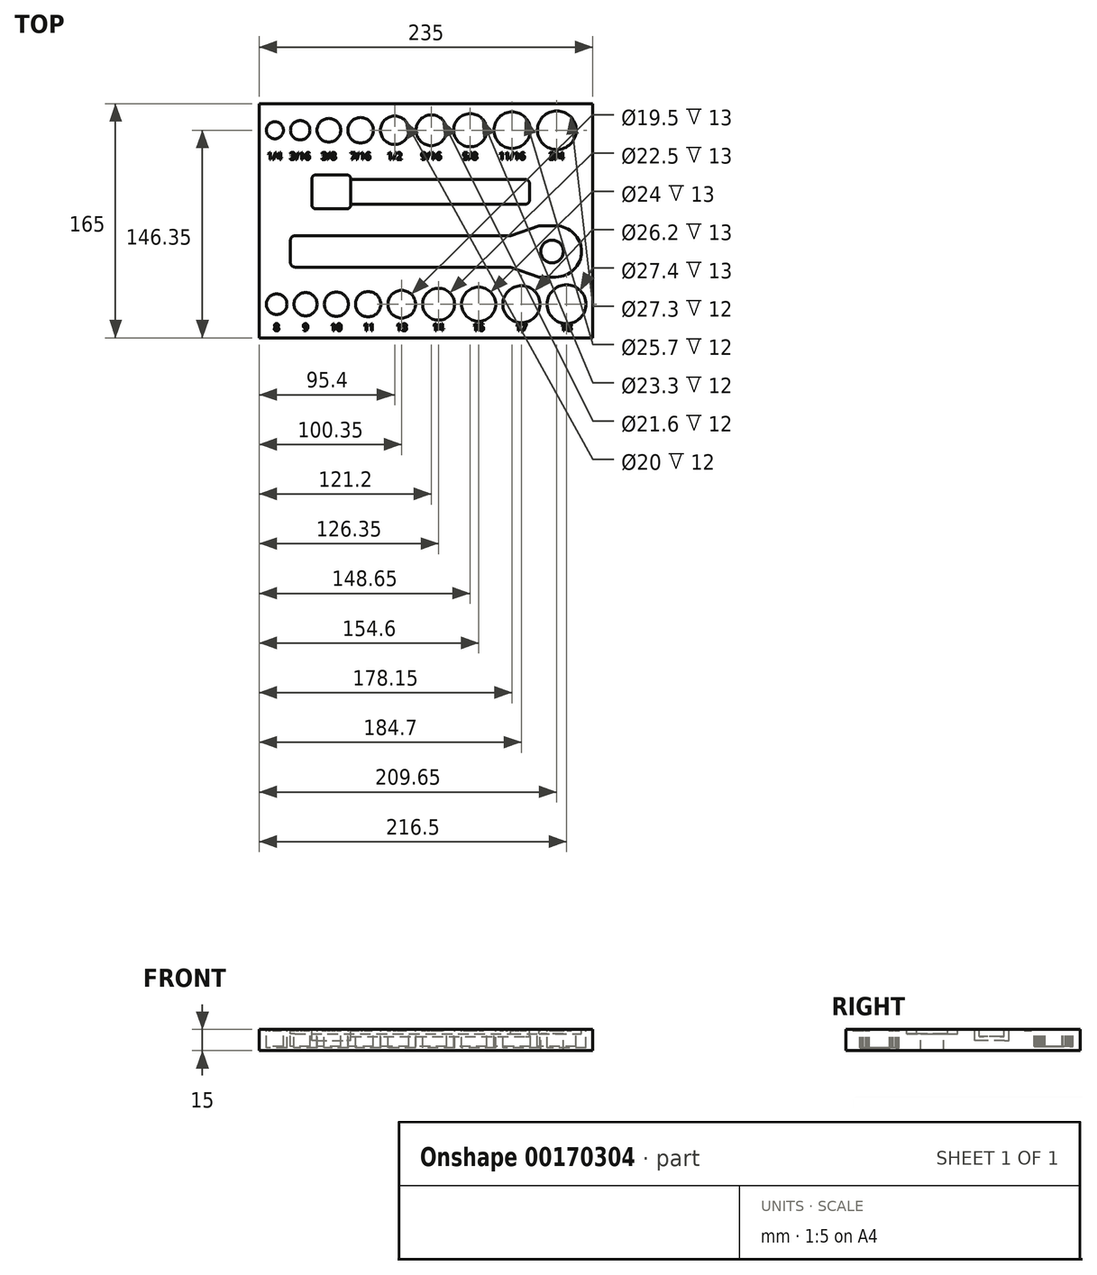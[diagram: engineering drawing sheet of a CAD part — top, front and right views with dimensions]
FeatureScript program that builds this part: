
annotation { "Feature Type Name" : "Feature", "Feature Type Description" : "" }
export const myFeature = defineFeature(function(context is Context, id is Id, definition is map)
    precondition{}
    {
        {
            var Q0;
            Q0=qCreatedBy(makeId("Top.planeOp"),FACE);
            var sketch = newSketch(context, id + "F0", { "sketchPlane" : qUnion([Q0])});
            skLineSegment(sketch, "E0.bottom", {"start": v(0, 0) * mm, "end": v(235, 0) * mm});
            skLineSegment(sketch, "E0.top", {"start": v(0, 165) * mm, "end": v(235, 165) * mm});
            skLineSegment(sketch, "E0.left", {"start": v(0, 0) * mm, "end": v(0, 165) * mm});
            skLineSegment(sketch, "E0.right", {"start": v(235, 0) * mm, "end": v(235, 165) * mm});
            skSolve(sketch);
        }
        {
            var Q0;
            Q0=makeQuery(id+"F0.imprint","IMPRINT",FACE,{"disambiguationData":[TD([[makeQuery(id+"F0.imprint","IMPRINT",EDGE,{"derivedFrom":sQuery(id+"F0.wireOp",EDGE,"E0.bottom")}),1.0]])]});
            extrude(context, id + "F1", {"entities" : qUnion([Q0]), "depth" : 15 * mm});
        }
        {
            var Q0;
            Q0=makeQuery(id+"F1.opExtrude","CAP_FACE",FACE,{"disambiguationData":[OSD([sQuery(id+"F0.wireOp",EDGE,"E0.bottom"),sQuery(id+"F0.wireOp",EDGE,"E0.top"),sQuery(id+"F0.wireOp",EDGE,"E0.left"),sQuery(id+"F0.wireOp",EDGE,"E0.right")])],"isStart":false});
            var sketch = newSketch(context, id + "F2", { "sketchPlane" : qUnion([Q0])});
            skLineSegment(sketch, "E1.bottom", {"start": v(0, 0) * mm, "end": v(12.25, 0) * mm, "construction": true});
            skLineSegment(sketch, "E1.top", {"start": v(0, 23.7) * mm, "end": v(12.25, 23.7) * mm, "construction": true});
            skLineSegment(sketch, "E1.left", {"start": v(0, 0) * mm, "end": v(0, 23.7) * mm, "construction": true});
            skLineSegment(sketch, "E1.right", {"start": v(12.25, 0) * mm, "end": v(12.25, 23.7) * mm, "construction": true});
            skLineSegment(sketch, "E2", {"start": v(12.25, 23.7) * mm, "end": v(32.65, 23.7) * mm, "construction": true});
            skLineSegment(sketch, "E3", {"start": v(32.65, 23.7) * mm, "end": v(54.3, 23.7) * mm, "construction": true});
            skPoint(sketch, "E3.endSnap0", {"position": v(22.45, 23.7) * mm});
            skLineSegment(sketch, "E4", {"start": v(54.3, 23.7) * mm, "end": v(76.7, 23.7) * mm, "construction": true});
            skLineSegment(sketch, "E5", {"start": v(76.7, 23.7) * mm, "end": v(100.35, 23.7) * mm, "construction": true});
            skLineSegment(sketch, "E6", {"start": v(100.35, 23.7) * mm, "end": v(126.35, 23.7) * mm, "construction": true});
            skLineSegment(sketch, "E7", {"start": v(126.35, 23.7) * mm, "end": v(154.6, 23.7) * mm, "construction": true});
            skLineSegment(sketch, "E8", {"start": v(154.6, 23.7) * mm, "end": v(184.7, 23.7) * mm, "construction": true});
            skLineSegment(sketch, "E9", {"start": v(184.7, 23.7) * mm, "end": v(216.5, 23.7) * mm, "construction": true});
            skCircle(sketch, "E10", {"center": v(12.25, 23.7) * mm, "radius": 7.25 * mm});
            skCircle(sketch, "E11", {"center": v(32.65, 23.7) * mm, "radius": 8.15 * mm});
            skCircle(sketch, "E12", {"center": v(54.3, 23.7) * mm, "radius": 8.5 * mm});
            skCircle(sketch, "E13", {"center": v(76.7, 23.7) * mm, "radius": 8.9 * mm});
            skCircle(sketch, "E14", {"center": v(100.35, 23.7) * mm, "radius": 9.75 * mm});
            skCircle(sketch, "E15", {"center": v(126.35, 23.7) * mm, "radius": 11.25 * mm});
            skCircle(sketch, "E16", {"center": v(154.6, 23.7) * mm, "radius": 12 * mm});
            skCircle(sketch, "E17", {"center": v(184.7, 23.7) * mm, "radius": 13.1 * mm});
            skCircle(sketch, "E18", {"center": v(216.5, 23.7) * mm, "radius": 13.7 * mm});
            skSolve(sketch);
        }
        {
            var Q0;
            Q0=makeQuery(id+"F2.imprint","IMPRINT",FACE,{"disambiguationData":[TD([[makeQuery(id+"F2.imprint","IMPRINT",EDGE,{"derivedFrom":sQuery(id+"F2.wireOp",EDGE,"E10")}),1.0]])]});
            var Q1;
            Q1=makeQuery(id+"F2.imprint","IMPRINT",FACE,{"disambiguationData":[TD([[makeQuery(id+"F2.imprint","IMPRINT",EDGE,{"derivedFrom":sQuery(id+"F2.wireOp",EDGE,"E18")}),1.0]])]});
            var Q2;
            Q2=makeQuery(id+"F2.imprint","IMPRINT",FACE,{"disambiguationData":[TD([[makeQuery(id+"F2.imprint","IMPRINT",EDGE,{"derivedFrom":sQuery(id+"F2.wireOp",EDGE,"E17")}),1.0]])]});
            var Q3;
            Q3=makeQuery(id+"F2.imprint","IMPRINT",FACE,{"disambiguationData":[TD([[makeQuery(id+"F2.imprint","IMPRINT",EDGE,{"derivedFrom":sQuery(id+"F2.wireOp",EDGE,"E16")}),1.0]])]});
            var Q4;
            Q4=makeQuery(id+"F2.imprint","IMPRINT",FACE,{"disambiguationData":[TD([[makeQuery(id+"F2.imprint","IMPRINT",EDGE,{"derivedFrom":sQuery(id+"F2.wireOp",EDGE,"E15")}),1.0]])]});
            var Q5;
            Q5=makeQuery(id+"F2.imprint","IMPRINT",FACE,{"disambiguationData":[TD([[makeQuery(id+"F2.imprint","IMPRINT",EDGE,{"derivedFrom":sQuery(id+"F2.wireOp",EDGE,"E14")}),1.0]])]});
            var Q6;
            Q6=makeQuery(id+"F2.imprint","IMPRINT",FACE,{"disambiguationData":[TD([[makeQuery(id+"F2.imprint","IMPRINT",EDGE,{"derivedFrom":sQuery(id+"F2.wireOp",EDGE,"E13")}),1.0]])]});
            var Q7;
            Q7=makeQuery(id+"F2.imprint","IMPRINT",FACE,{"disambiguationData":[TD([[makeQuery(id+"F2.imprint","IMPRINT",EDGE,{"derivedFrom":sQuery(id+"F2.wireOp",EDGE,"E12")}),1.0]])]});
            var Q8;
            Q8=makeQuery(id+"F2.imprint","IMPRINT",FACE,{"disambiguationData":[TD([[makeQuery(id+"F2.imprint","IMPRINT",EDGE,{"derivedFrom":sQuery(id+"F2.wireOp",EDGE,"E11")}),1.0]])]});
            extrude(context, id + "F3", {"entities" : qUnion([Q0, Q1, Q2, Q3, Q4, Q5, Q6, Q7, Q8]), "operationType" : NewBodyOperationType.REMOVE, "oppositeDirection" : true, "depth" : 13 * mm});
        }
        {
            var Q0;
            Q0=makeQuery(id+"F1.opExtrude","CAP_FACE",FACE,{"disambiguationData":[OSD([sQuery(id+"F0.wireOp",EDGE,"E0.bottom"),sQuery(id+"F0.wireOp",EDGE,"E0.top"),sQuery(id+"F0.wireOp",EDGE,"E0.left"),sQuery(id+"F0.wireOp",EDGE,"E0.right")])],"isStart":false});
            var sketch = newSketch(context, id + "F4", { "sketchPlane" : qUnion([Q0])});
            skLineSegment(sketch, "E19", {"start": v(0, 0) * mm, "end": v(0, 3) * mm, "construction": true});
            skLineSegment(sketch, "E20", {"start": v(0, 3) * mm, "end": v(235, 3) * mm, "construction": true});
            skLineSegment(sketch, "E21", {"start": v(235, 3) * mm, "end": v(216.5, 23.7) * mm, "construction": true});
            skLineSegment(sketch, "E22", {"start": v(216.5, 23.7) * mm, "end": v(216.5, 3) * mm, "construction": true});
            skLineSegment(sketch, "E23", {"start": v(216.5, 3) * mm, "end": v(184.7, 23.7) * mm, "construction": true});
            skLineSegment(sketch, "E24", {"start": v(184.7, 23.7) * mm, "end": v(184.7, 3) * mm, "construction": true});
            skLineSegment(sketch, "E25", {"start": v(184.7, 3) * mm, "end": v(154.6, 23.7) * mm, "construction": true});
            skLineSegment(sketch, "E26", {"start": v(154.6, 23.7) * mm, "end": v(154.6, 3) * mm, "construction": true});
            skLineSegment(sketch, "E27", {"start": v(154.6, 3) * mm, "end": v(126.35, 23.7) * mm, "construction": true});
            skLineSegment(sketch, "E28", {"start": v(126.35, 23.7) * mm, "end": v(126.35, 3) * mm, "construction": true});
            skLineSegment(sketch, "E29", {"start": v(126.35, 3) * mm, "end": v(100.35, 23.7) * mm, "construction": true});
            skLineSegment(sketch, "E30", {"start": v(100.35, 23.7) * mm, "end": v(100.35, 3) * mm, "construction": true});
            skLineSegment(sketch, "E31", {"start": v(100.35, 3) * mm, "end": v(76.7, 23.7) * mm, "construction": true});
            skLineSegment(sketch, "E32", {"start": v(76.7, 23.7) * mm, "end": v(76.7, 3) * mm, "construction": true});
            skLineSegment(sketch, "E33", {"start": v(76.7, 3) * mm, "end": v(54.3, 23.7) * mm, "construction": true});
            skLineSegment(sketch, "E34", {"start": v(54.3, 23.7) * mm, "end": v(54.3, 3) * mm, "construction": true});
            skLineSegment(sketch, "E35", {"start": v(54.3, 3) * mm, "end": v(32.65, 23.7) * mm, "construction": true});
            skLineSegment(sketch, "E36", {"start": v(32.65, 23.7) * mm, "end": v(32.65, 3) * mm, "construction": true});
            skLineSegment(sketch, "E37", {"start": v(32.65, 3) * mm, "end": v(12.25, 23.7) * mm, "construction": true});
            skLineSegment(sketch, "E38", {"start": v(12.25, 23.7) * mm, "end": v(12.25, 3) * mm, "construction": true});
            skSolve(sketch);
        }
        {
            var Q0;
            Q0=makeQuery(id+"F4.imprint","IMPRINT",FACE,{"disambiguationData":[TD([[makeQuery(id+"F4.imprint","IMPRINT",EDGE,{"derivedFrom":makeQuery(id+"F1.opExtrude","CAP_EDGE",EDGE,{"disambiguationData":[OSD([sQuery(id+"F0.wireOp",EDGE,"E0.bottom")])],"isStart":false})}),1.0]])]});
            var sketch = newSketch(context, id + "F5", { "sketchPlane" : qUnion([Q0])});
            skText(sketch, "E39", { "text": "8", "fontName": "OpenSans-Regular.ttf"});
            skText(sketch, "E40", { "text": "9", "fontName": "OpenSans-Regular.ttf"});
            skText(sketch, "E41", { "text": "10", "fontName": "OpenSans-Regular.ttf"});
            skText(sketch, "E42", { "text": "11", "fontName": "OpenSans-Regular.ttf"});
            skText(sketch, "E43", { "text": "13", "fontName": "OpenSans-Regular.ttf"});
            skText(sketch, "E44", { "text": "14", "fontName": "OpenSans-Regular.ttf"});
            skText(sketch, "E45", { "text": "16", "fontName": "OpenSans-Regular.ttf"});
            skText(sketch, "E46", { "text": "17", "fontName": "OpenSans-Regular.ttf"});
            skText(sketch, "E47", { "text": "18", "fontName": "OpenSans-Regular.ttf"});
            const initialGuessF5  = {"E39": [0.01022, 0.005, 1, 0, 0.005], "E40": [0.03063, 0.005, 1, 0, 0.005], "E41": [0.05028, 0.005, 1, 0, 0.005], "E42": [0.07328, 0.005, 1, 0, 0.005], "E43": [0.09636, 0.005, 1, 0, 0.005], "E44": [0.12222, 0.005, 1, 0, 0.005], "E45": [0.15057, 0.005, 1, 0, 0.005], "E46": [0.18068, 0.005, 1, 0, 0.005], "E47": [0.21248, 0.005, 1, 0, 0.005]};
            skSetInitialGuess(sketch, initialGuessF5);
            skSolve(sketch);
        }
        {
            var Q0;
            Q0 = qSketchRegion(id + "F5", true);
            extrude(context, id + "F6", {"entities" : qUnion([Q0]), "operationType" : NewBodyOperationType.REMOVE, "oppositeDirection" : true, "depth" : 1 * mm});
        }
        {
            var Q0;
            Q0=makeQuery(id+"F4.imprint","IMPRINT",FACE,{"disambiguationData":[TD([[makeQuery(id+"F4.imprint","IMPRINT",EDGE,{"derivedFrom":makeQuery(id+"F1.opExtrude","CAP_EDGE",EDGE,{"disambiguationData":[OSD([sQuery(id+"F0.wireOp",EDGE,"E0.bottom")])],"isStart":false})}),1.0]])]});
            var sketch = newSketch(context, id + "F7", { "sketchPlane" : qUnion([Q0])});
            skCircle(sketch, "E48.0", {"center": v(12.25, 23.7) * mm, "radius": 7.25 * mm});
            skLineSegment(sketch, "E49", {"start": v(12.25, 23.7) * mm, "end": v(0, 23.7) * mm, "construction": true});
            skLineSegment(sketch, "E50", {"start": v(0, 23.7) * mm, "end": v(0, 60.9) * mm, "construction": true});
            skLineSegment(sketch, "E51", {"start": v(0, 60.9) * mm, "end": v(22, 60.9) * mm, "construction": true});
            skLineSegment(sketch, "E52.top", {"start": v(25, 71.9) * mm, "end": v(177, 71.9) * mm});
            skLineSegment(sketch, "E52.left", {"start": v(22, 60.9) * mm, "end": v(22, 68.9) * mm});
            skLineSegment(sketch, "E53.bottom", {"start": v(194.75, 71.9) * mm, "end": v(197, 71.9) * mm, "construction": true});
            skLineSegment(sketch, "E53.top", {"start": v(177, 78.9) * mm, "end": v(197, 78.9) * mm, "construction": true});
            skLineSegment(sketch, "E54", {"start": v(177, 71.9) * mm, "end": v(197, 78.9) * mm});
            skLineSegment(sketch, "E55", {"start": v(197, 78.9) * mm, "end": v(209, 78.9) * mm});
            skArc(sketch, "E56", {"start": v(227, 60.9) * mm, "mid": v(221.73, 73.63) * mm, "end": v(209, 78.9) * mm});
            skLineSegment(sketch, "E57.MirrorCS", {"start": v(22, 60.9) * mm, "end": v(22, 52.9) * mm});
            skLineSegment(sketch, "E58.MirrorCS", {"start": v(25, 49.9) * mm, "end": v(177, 49.9) * mm});
            skLineSegment(sketch, "E59.MirrorCS", {"start": v(177, 49.9) * mm, "end": v(197, 42.9) * mm});
            skLineSegment(sketch, "E60.MirrorCS", {"start": v(197, 42.9) * mm, "end": v(209, 42.9) * mm});
            skArc(sketch, "E61.MirrorCS", {"start": v(227, 60.9) * mm, "mid": v(221.73, 48.17) * mm, "end": v(209, 42.9) * mm});
            skPoint(sketch, "E62.visualSharp", {"position": v(22, 71.9) * mm});
            skArc(sketch, "E62.filletArc", {"start": v(25, 71.9) * mm, "mid": v(22.88, 71.02) * mm, "end": v(22, 68.9) * mm});
            skPoint(sketch, "E63.visualSharp", {"position": v(22, 49.9) * mm});
            skArc(sketch, "E63.filletArc", {"start": v(22, 52.9) * mm, "mid": v(22.88, 50.78) * mm, "end": v(25, 49.9) * mm});
            skLineSegment(sketch, "E64", {"start": v(227, 60.9) * mm, "end": v(206.25, 60.9) * mm, "construction": true});
            skCircle(sketch, "E65", {"center": v(206.25, 60.9) * mm, "radius": 8 * mm});
            skLineSegment(sketch, "E66", {"start": v(25, 71.9) * mm, "end": v(85, 71.9) * mm, "construction": true});
            skLineSegment(sketch, "E67.bottom", {"start": v(85, 71.9) * mm, "end": v(135, 71.9) * mm});
            skPoint(sketch, "E68.visualSharp", {"position": v(85, 81.9) * mm});
            skPoint(sketch, "E69.visualSharp", {"position": v(135, 81.9) * mm});
            skLineSegment(sketch, "E70", {"start": v(22, 60.9) * mm, "end": v(206.25, 60.9) * mm, "construction": true});
            skSolve(sketch);
        }
        {
            var Q0;
            Q0 = qSketchRegion(id + "F7", true);
            extrude(context, id + "F8", {"entities" : qUnion([Q0]), "operationType" : NewBodyOperationType.REMOVE, "oppositeDirection" : true, "depth" : 3 * mm});
        }
        {
            var Q0;
            Q0=makeQuery(id+"F4.imprint","IMPRINT",FACE,{"disambiguationData":[TD([[makeQuery(id+"F4.imprint","IMPRINT",EDGE,{"derivedFrom":makeQuery(id+"F1.opExtrude","CAP_EDGE",EDGE,{"disambiguationData":[OSD([sQuery(id+"F0.wireOp",EDGE,"E0.bottom")])],"isStart":false})}),1.0]])]});
            var sketch = newSketch(context, id + "F9", { "sketchPlane" : qUnion([Q0])});
            skCircle(sketch, "E71.0", {"center": v(206.25, 60.9) * mm, "radius": 8 * mm});
            skCircle(sketch, "E72", {"center": v(206.25, 60.9) * mm, "radius": 8.25 * mm});
            skSolve(sketch);
        }
        {
            var Q0;
            Q0=makeQuery(id+"F9.imprint","IMPRINT",FACE,{"disambiguationData":[TD([[makeQuery(id+"F9.imprint","IMPRINT",EDGE,{"derivedFrom":sQuery(id+"F9.wireOp",EDGE,"E71.0")}),1.0]])]});
            extrude(context, id + "F10", {"entities" : qUnion([Q0]), "operationType" : NewBodyOperationType.REMOVE, "oppositeDirection" : true, "depth" : 25 * mm});
        }
        {
            var Q0;
            Q0=makeQuery(id+"F4.imprint","IMPRINT",FACE,{"disambiguationData":[TD([[makeQuery(id+"F4.imprint","IMPRINT",EDGE,{"derivedFrom":makeQuery(id+"F1.opExtrude","CAP_EDGE",EDGE,{"disambiguationData":[OSD([sQuery(id+"F0.wireOp",EDGE,"E0.bottom")])],"isStart":false})}),1.0]])]});
            var sketch = newSketch(context, id + "F11", { "sketchPlane" : qUnion([Q0])});
            skPoint(sketch, "E73.0", {"position": v(22, 60.9) * mm});
            skLineSegment(sketch, "E74", {"start": v(22, 60.9) * mm, "end": v(0, 60.9) * mm, "construction": true});
            skLineSegment(sketch, "E75", {"start": v(0, 60.9) * mm, "end": v(0, 102.9) * mm, "construction": true});
            skLineSegment(sketch, "E76", {"start": v(0, 102.9) * mm, "end": v(37, 102.9) * mm, "construction": true});
            skLineSegment(sketch, "E77", {"start": v(190.5, 102.9) * mm, "end": v(239.14, 102.9) * mm, "construction": true});
            skLineSegment(sketch, "E78.top", {"start": v(40, 114.9) * mm, "end": v(61.5, 114.9) * mm});
            skLineSegment(sketch, "E78.left", {"start": v(37, 102.9) * mm, "end": v(37, 111.9) * mm});
            skLineSegment(sketch, "E78.right", {"start": v(64.5, 111.65) * mm, "end": v(64.5, 111.9) * mm});
            skLineSegment(sketch, "E79.top", {"start": v(64.5, 111.65) * mm, "end": v(187.5, 111.65) * mm});
            skLineSegment(sketch, "E79.right", {"start": v(190.5, 102.9) * mm, "end": v(190.5, 108.65) * mm});
            skPoint(sketch, "E80.visualSharp", {"position": v(64.5, 114.9) * mm});
            skArc(sketch, "E80.filletArc", {"start": v(64.5, 111.9) * mm, "mid": v(63.62, 114.02) * mm, "end": v(61.5, 114.9) * mm});
            skPoint(sketch, "E81.visualSharp", {"position": v(37, 114.9) * mm});
            skArc(sketch, "E81.filletArc", {"start": v(40, 114.9) * mm, "mid": v(37.88, 114.02) * mm, "end": v(37, 111.9) * mm});
            skPoint(sketch, "E82.visualSharp", {"position": v(190.5, 111.65) * mm});
            skArc(sketch, "E82.filletArc", {"start": v(190.5, 108.65) * mm, "mid": v(189.62, 110.77) * mm, "end": v(187.5, 111.65) * mm});
            skLineSegment(sketch, "E83.MirrorCS", {"start": v(37, 102.9) * mm, "end": v(37, 93.9) * mm});
            skArc(sketch, "E84.MirrorCS", {"start": v(40, 90.9) * mm, "mid": v(37.88, 91.78) * mm, "end": v(37, 93.9) * mm});
            skLineSegment(sketch, "E85.MirrorCS", {"start": v(40, 90.9) * mm, "end": v(61.5, 90.9) * mm});
            skArc(sketch, "E86.MirrorCS", {"start": v(64.5, 93.9) * mm, "mid": v(63.62, 91.78) * mm, "end": v(61.5, 90.9) * mm});
            skLineSegment(sketch, "E87.MirrorCS", {"start": v(64.5, 94.15) * mm, "end": v(64.5, 93.9) * mm});
            skLineSegment(sketch, "E88.MirrorCS", {"start": v(64.5, 94.15) * mm, "end": v(187.5, 94.15) * mm});
            skArc(sketch, "E89.MirrorCS", {"start": v(190.5, 97.15) * mm, "mid": v(189.62, 95.03) * mm, "end": v(187.5, 94.15) * mm});
            skLineSegment(sketch, "E90.MirrorCS", {"start": v(190.5, 102.9) * mm, "end": v(190.5, 97.15) * mm});
            skSolve(sketch);
        }
        {
            var Q0;
            Q0 = qSketchRegion(id + "F11", true);
            extrude(context, id + "F12", {"entities" : qUnion([Q0]), "operationType" : NewBodyOperationType.REMOVE, "oppositeDirection" : true, "depth" : 5 * mm});
        }
        {
            var Q0;
            Q0=makeQuery(id+"F4.imprint","IMPRINT",FACE,{"disambiguationData":[TD([[makeQuery(id+"F4.imprint","IMPRINT",EDGE,{"derivedFrom":makeQuery(id+"F1.opExtrude","CAP_EDGE",EDGE,{"disambiguationData":[OSD([sQuery(id+"F0.wireOp",EDGE,"E0.bottom")])],"isStart":false})}),1.0]])]});
            var sketch = newSketch(context, id + "F13", { "sketchPlane" : qUnion([Q0])});
            skLineSegment(sketch, "E91.top", {"start": v(5, 146.35) * mm, "end": v(11, 146.35) * mm, "construction": true});
            skLineSegment(sketch, "E92.0.1", {"start": v(0, 0) * mm, "end": v(235, 0) * mm});
            skLineSegment(sketch, "E92.0.2", {"start": v(235, 0) * mm, "end": v(235, 165) * mm});
            skLineSegment(sketch, "E92.0.3", {"start": v(235, 165) * mm, "end": v(0, 165) * mm});
            skLineSegment(sketch, "E93", {"start": v(11, 146.35) * mm, "end": v(28.85, 146.35) * mm, "construction": true});
            skLineSegment(sketch, "E94", {"start": v(28.85, 146.35) * mm, "end": v(49.05, 146.35) * mm, "construction": true});
            skLineSegment(sketch, "E95", {"start": v(49.05, 146.35) * mm, "end": v(71.4, 146.35) * mm, "construction": true});
            skLineSegment(sketch, "E96", {"start": v(71.4, 146.35) * mm, "end": v(95.4, 146.35) * mm, "construction": true});
            skLineSegment(sketch, "E97", {"start": v(95.4, 146.35) * mm, "end": v(121.2, 146.35) * mm, "construction": true});
            skLineSegment(sketch, "E98", {"start": v(121.2, 146.35) * mm, "end": v(148.65, 146.35) * mm, "construction": true});
            skLineSegment(sketch, "E99", {"start": v(148.65, 146.35) * mm, "end": v(178.15, 146.35) * mm, "construction": true});
            skLineSegment(sketch, "E100", {"start": v(178.15, 146.35) * mm, "end": v(209.65, 146.35) * mm, "construction": true});
            skCircle(sketch, "E101", {"center": v(11, 146.35) * mm, "radius": 6 * mm});
            skCircle(sketch, "E102", {"center": v(28.85, 146.35) * mm, "radius": 6.85 * mm});
            skCircle(sketch, "E103", {"center": v(49.05, 146.35) * mm, "radius": 8.35 * mm});
            skCircle(sketch, "E104", {"center": v(71.4, 146.35) * mm, "radius": 9 * mm});
            skCircle(sketch, "E105", {"center": v(95.4, 146.35) * mm, "radius": 10 * mm});
            skCircle(sketch, "E106", {"center": v(121.2, 146.35) * mm, "radius": 10.8 * mm});
            skCircle(sketch, "E107", {"center": v(148.65, 146.35) * mm, "radius": 11.65 * mm});
            skCircle(sketch, "E108", {"center": v(178.15, 146.35) * mm, "radius": 12.85 * mm});
            skCircle(sketch, "E109", {"center": v(209.65, 146.35) * mm, "radius": 13.65 * mm});
            skSolve(sketch);
        }
        {
            var Q0;
            Q0 = qSketchRegion(id + "F13", true);
            extrude(context, id + "F14", {"entities" : qUnion([Q0]), "operationType" : NewBodyOperationType.REMOVE, "oppositeDirection" : true, "depth" : 12 * mm});
        }
        {
            var Q0;
            Q0=makeQuery(id+"F4.imprint","IMPRINT",FACE,{"disambiguationData":[TD([[makeQuery(id+"F4.imprint","IMPRINT",EDGE,{"derivedFrom":makeQuery(id+"F1.opExtrude","CAP_EDGE",EDGE,{"disambiguationData":[OSD([sQuery(id+"F0.wireOp",EDGE,"E0.bottom")])],"isStart":false})}),1.0]])]});
            var sketch = newSketch(context, id + "F15", { "sketchPlane" : qUnion([Q0])});
            skLineSegment(sketch, "E110.0.1", {"start": v(0, 0) * mm, "end": v(235, 0) * mm});
            skLineSegment(sketch, "E110.0.2", {"start": v(235, 0) * mm, "end": v(235, 165) * mm});
            skCircle(sketch, "E111.0", {"center": v(11, 146.35) * mm, "radius": 6 * mm, "construction": true});
            skCircle(sketch, "E111.1", {"center": v(28.85, 146.35) * mm, "radius": 6.85 * mm, "construction": true});
            skCircle(sketch, "E111.2", {"center": v(49.05, 146.35) * mm, "radius": 8.35 * mm, "construction": true});
            skCircle(sketch, "E111.3", {"center": v(71.4, 146.35) * mm, "radius": 9 * mm, "construction": true});
            skCircle(sketch, "E111.4", {"center": v(95.4, 146.35) * mm, "radius": 10 * mm, "construction": true});
            skCircle(sketch, "E111.5", {"center": v(121.2, 146.35) * mm, "radius": 10.8 * mm, "construction": true});
            skCircle(sketch, "E111.6", {"center": v(148.65, 146.35) * mm, "radius": 11.65 * mm, "construction": true});
            skCircle(sketch, "E111.7", {"center": v(178.15, 146.35) * mm, "radius": 12.85 * mm, "construction": true});
            skCircle(sketch, "E111.8", {"center": v(209.65, 146.35) * mm, "radius": 13.65 * mm, "construction": true});
            skLineSegment(sketch, "E112", {"start": v(0, 125.7) * mm, "end": v(11, 146.35) * mm, "construction": true});
            skLineSegment(sketch, "E113", {"start": v(11, 125.7) * mm, "end": v(28.85, 146.35) * mm, "construction": true});
            skLineSegment(sketch, "E114", {"start": v(28.85, 125.7) * mm, "end": v(49.05, 146.35) * mm, "construction": true});
            skLineSegment(sketch, "E115", {"start": v(49.05, 125.7) * mm, "end": v(71.4, 146.35) * mm, "construction": true});
            skLineSegment(sketch, "E116", {"start": v(71.4, 125.7) * mm, "end": v(95.4, 146.35) * mm, "construction": true});
            skLineSegment(sketch, "E117", {"start": v(95.4, 125.7) * mm, "end": v(121.2, 146.35) * mm, "construction": true});
            skLineSegment(sketch, "E118", {"start": v(121.2, 125.7) * mm, "end": v(148.65, 146.35) * mm, "construction": true});
            skLineSegment(sketch, "E119", {"start": v(148.65, 125.7) * mm, "end": v(178.15, 146.35) * mm, "construction": true});
            skLineSegment(sketch, "E120", {"start": v(178.15, 125.7) * mm, "end": v(209.65, 146.35) * mm, "construction": true});
            skLineSegment(sketch, "E121", {"start": v(209.65, 146.35) * mm, "end": v(209.65, 125.7) * mm, "construction": true});
            skText(sketch, "E122", { "text": "1/4", "fontName": "OpenSans-Regular.ttf"});
            skText(sketch, "E123", { "text": "3/16", "fontName": "OpenSans-Regular.ttf"});
            skText(sketch, "E124", { "text": "3/8", "fontName": "OpenSans-Regular.ttf"});
            skText(sketch, "E125", { "text": "7/16", "fontName": "OpenSans-Regular.ttf"});
            skText(sketch, "E126", { "text": "1/2", "fontName": "OpenSans-Regular.ttf"});
            skText(sketch, "E127", { "text": "9/16", "fontName": "OpenSans-Regular.ttf"});
            skText(sketch, "E128", { "text": "5/8", "fontName": "OpenSans-Regular.ttf"});
            skText(sketch, "E129", { "text": "11/16", "fontName": "OpenSans-Regular.ttf"});
            skText(sketch, "E130", { "text": "3/4\n", "fontName": "OpenSans-Regular.ttf"});
            const initialGuessF15  = {"E122": [0.0056, 0.1257, 1, 0, 0.005], "E123": [0.02156, 0.1257, 1, 0, 0.005], "E124": [0.04376, 0.1257, 1, 0, 0.005], "E125": [0.06411, 0.1257, 1, 0, 0.005], "E126": [0.09012, 0.1257, 1, 0, 0.005], "E127": [0.11391, 0.1257, 1, 0, 0.005], "E128": [0.14336, 0.1257, 1, 0, 0.005], "E129": [0.16888, 0.1257, 1, 0, 0.005], "E130": [0.20425, 0.1257, 1, 0, 0.005]};
            skSetInitialGuess(sketch, initialGuessF15);
            skSolve(sketch);
        }
        {
            var Q0;
            Q0 = qSketchRegion(id + "F15", true);
            extrude(context, id + "F16", {"entities" : qUnion([Q0]), "operationType" : NewBodyOperationType.REMOVE, "oppositeDirection" : true, "depth" : 1 * mm});
        }
        {
            var Q0;
            Q0=makeQuery(id+"F4.imprint","IMPRINT",FACE,{"disambiguationData":[TD([[makeQuery(id+"F4.imprint","IMPRINT",EDGE,{"derivedFrom":makeQuery(id+"F1.opExtrude","CAP_EDGE",EDGE,{"disambiguationData":[OSD([sQuery(id+"F0.wireOp",EDGE,"E0.bottom")])],"isStart":false})}),1.0]])]});
            var sketch = newSketch(context, id + "F17", { "sketchPlane" : qUnion([Q0])});
            skLineSegment(sketch, "E131.0", {"start": v(40, 114.9) * mm, "end": v(61.5, 114.9) * mm});
            skArc(sketch, "E132.0", {"start": v(40, 114.9) * mm, "mid": v(37.88, 114.02) * mm, "end": v(37, 111.9) * mm});
            skLineSegment(sketch, "E133.0", {"start": v(37, 93.9) * mm, "end": v(37, 111.9) * mm});
            skArc(sketch, "E134.0", {"start": v(40, 90.9) * mm, "mid": v(37.88, 91.78) * mm, "end": v(37, 93.9) * mm});
            skLineSegment(sketch, "E135.0", {"start": v(40, 90.9) * mm, "end": v(61.5, 90.9) * mm});
            skArc(sketch, "E136.0", {"start": v(64.5, 93.9) * mm, "mid": v(63.62, 91.78) * mm, "end": v(61.5, 90.9) * mm});
            skLineSegment(sketch, "E137.0", {"start": v(64.5, 94.15) * mm, "end": v(64.5, 93.9) * mm});
            skArc(sketch, "E138.0", {"start": v(64.5, 111.9) * mm, "mid": v(63.62, 114.02) * mm, "end": v(61.5, 114.9) * mm});
            skLineSegment(sketch, "E139.0", {"start": v(64.5, 111.65) * mm, "end": v(64.5, 111.9) * mm});
            skLineSegment(sketch, "E140", {"start": v(64.5, 111.65) * mm, "end": v(64.5, 94.15) * mm});
            skSolve(sketch);
        }
        {
            var Q0;
            Q0 = qSketchRegion(id + "F17", true);
            extrude(context, id + "F18", {"entities" : qUnion([Q0]), "operationType" : NewBodyOperationType.REMOVE, "oppositeDirection" : true, "depth" : 8 * mm});
        }
    });
